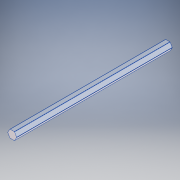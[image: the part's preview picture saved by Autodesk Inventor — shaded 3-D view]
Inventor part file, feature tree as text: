
AUTODESK INVENTOR PART (.ipt)
format: ipt  version: 2016 (Build 200138000, 138)  size: 140,288 bytes
history: native  units: in
note: dims shown in document units (in); Inventor stores cm internally (conversion verified against a paired STEP export)
features: fillet x1, other x1, extrude x1, imported_body x1, sketch x1
ambient origin geometry x8: Origin, YZ Plane, XZ Plane, XY Plane, X Axis, Y Axis, Z Axis, Center Point
bodies: Body1 (feature_tree)
feature tree (5):
  fillet  "Fillet1"  Radius=8.0in
  other  "18inShaft1"
  extrude  "Extrusion1"  [1 undecoded]
  imported_body  "Base1"
  sketch  "Sketch1"
note: 1 required parameter value undecoded (feature->parameter linkage not recoverable at this tier; creation-order binding heuristic only, values carry confidence <= 0.55)
